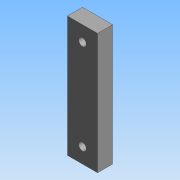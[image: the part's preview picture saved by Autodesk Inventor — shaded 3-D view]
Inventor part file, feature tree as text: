
AUTODESK INVENTOR PART (.ipt)
format: ipt  version: 2015 (Build 190159000, 159)  size: 86,528 bytes
history: native  units: mm
features: extrude x2, sketch x1, projected_geometry x1
ambient origin geometry x8: Origin, YZ Plane, XZ Plane, XY Plane, X Axis, Y Axis, Z Axis, Center Point
bodies: Solid1 (feature_tree)
feature tree (4):
  extrude  "Extrusion1"  Depth=10.0mm TaperAngle=0.0deg
  extrude  "Extrusion2"  Depth=20.0mm
  sketch  "Sketch5"  dims[d0=80.0mm d1=10.0mm d2=0.0mm d3=20.0mm d4=5.0mm d5=5.0mm d6=5.0mm d7=10.0mm d8=10.0mm d9=10.0mm d10=10.0mm d11=10.0mm d12=0.0mm]
  projected_geometry  "Projected Loop1"
